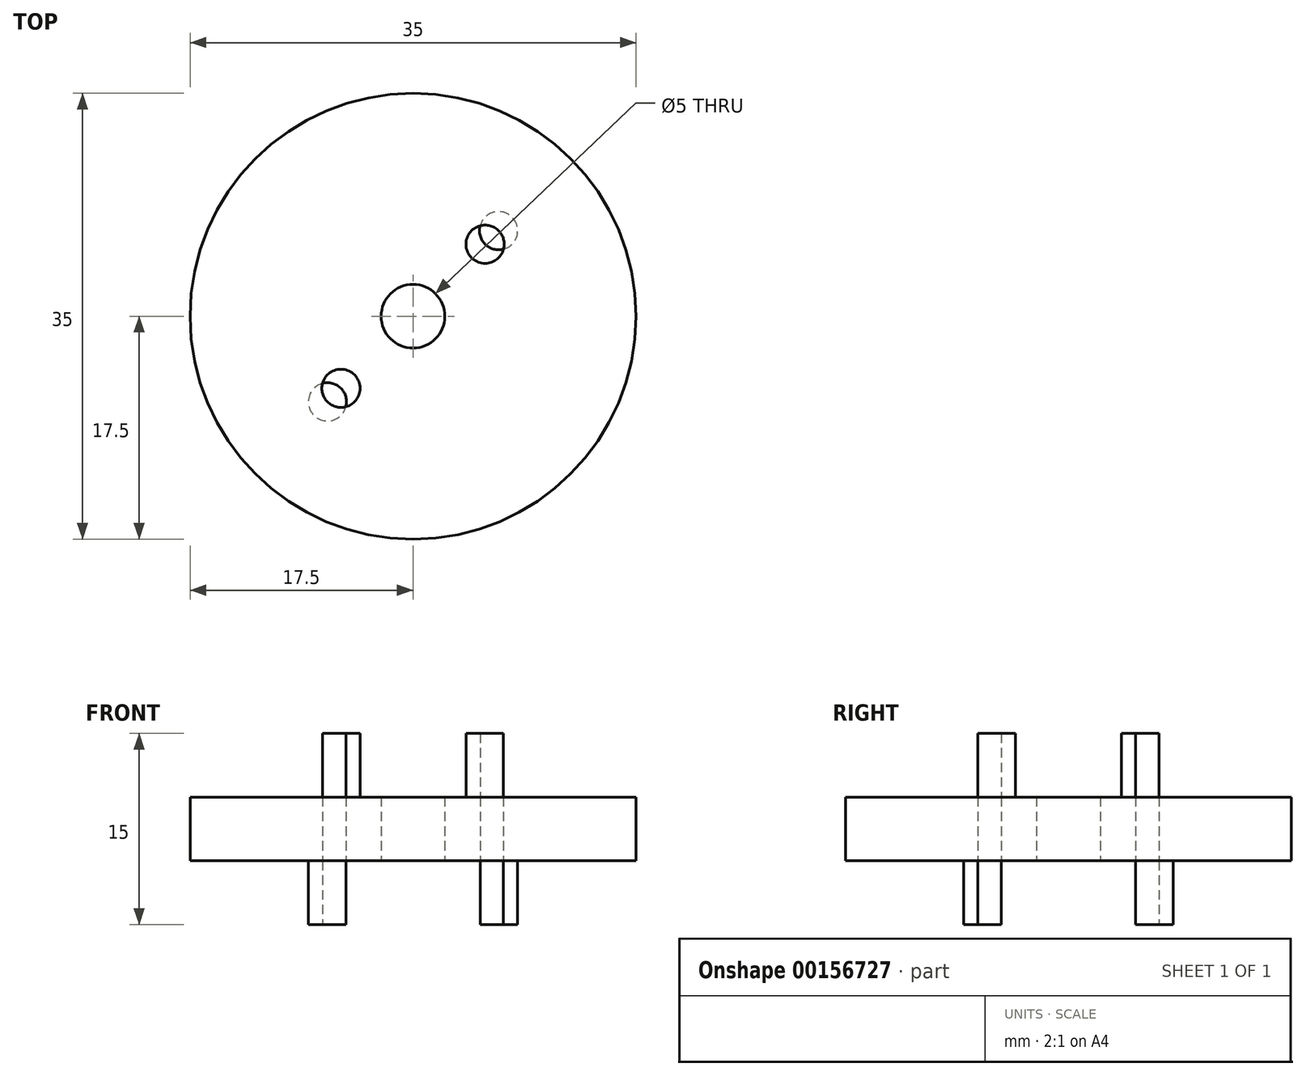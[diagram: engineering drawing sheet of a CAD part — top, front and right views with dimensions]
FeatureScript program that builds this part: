
annotation { "Feature Type Name" : "Feature", "Feature Type Description" : "" }
export const myFeature = defineFeature(function(context is Context, id is Id, definition is map)
    precondition{}
    {
        {
            var Q0;
            Q0=qCreatedBy(makeId("Top.planeOp"),FACE);
            var sketch = newSketch(context, id + "F0", { "sketchPlane" : qUnion([Q0])});
            skCircle(sketch, "E0", {"center": v(0, 0) * mm, "radius": 17.5 * mm});
            skCircle(sketch, "E1", {"center": v(0, 0) * mm, "radius": 2.5 * mm});
            skCircle(sketch, "E2", {"center": v(-5.66, 5.66) * mm, "radius": 1.5 * mm});
            skLineSegment(sketch, "E3", {"start": v(-5.66, 5.66) * mm, "end": v(0, 0) * mm, "construction": true});
            skCircle(sketch, "E4.MirrorC", {"center": v(5.66, 5.66) * mm, "radius": 1.5 * mm});
            skCircle(sketch, "E5.MirrorC", {"center": v(5.66, -5.66) * mm, "radius": 1.5 * mm});
            skCircle(sketch, "E6.MirrorC", {"center": v(-5.66, -5.66) * mm, "radius": 1.5 * mm});
            skCircle(sketch, "E7", {"center": v(0, 0) * mm, "radius": 9.5 * mm, "construction": true});
            skLineSegment(sketch, "E8", {"start": v(0, 0) * mm, "end": v(14.34, 14.34) * mm, "construction": true});
            skCircle(sketch, "E9", {"center": v(6.72, 6.72) * mm, "radius": 1.5 * mm});
            skCircle(sketch, "E10.MirrorC", {"center": v(-6.72, -6.72) * mm, "radius": 1.5 * mm});
            skSolve(sketch);
        }
        {
            var Q0;
            Q0=makeQuery(id+"F0.imprint","IMPRINT",FACE,{"disambiguationData":[TD([[makeQuery(id+"F0.imprint","IMPRINT",EDGE,{"derivedFrom":sQuery(id+"F0.wireOp",EDGE,"E0")}),1.0]])]});
            var Q1;
            Q1=makeQuery(id+"F0.imprint","IMPRINT",FACE,{"disambiguationData":[TD([[makeQuery(id+"F0.imprint","IMPRINT",EDGE,{"derivedFrom":sQuery(id+"F0.wireOp",EDGE,"E2")}),1.0]])]});
            var Q2;
            {var subQ0=sQuery(id+"F0.wireOp",EDGE,"E10.MirrorC");var subQ1=sQuery(id+"F0.wireOp",EDGE,"E6.MirrorC");var subQ2=makeQuery(id+"F0.imprint","INTERSECT",VERTEX,{"disambiguationData":[OD(0.0)],"derivedFrom":[subQ1,subQ0]});Q2=makeQuery(id+"F0.imprint","IMPRINT",FACE,{"disambiguationData":[TD([[makeQuery(id+"F0.imprint","IMPRINT",EDGE,{"disambiguationData":[TD([[subQ2,1.0]])],"derivedFrom":subQ1}),1.0]])]});}
            var Q3;
            {var subQ0=sQuery(id+"F0.wireOp",EDGE,"E10.MirrorC");var subQ1=sQuery(id+"F0.wireOp",EDGE,"E6.MirrorC");var subQ2=makeQuery(id+"F0.imprint","INTERSECT",VERTEX,{"disambiguationData":[OD(0.0)],"derivedFrom":[subQ1,subQ0]});Q3=makeQuery(id+"F0.imprint","IMPRINT",FACE,{"disambiguationData":[TD([[makeQuery(id+"F0.imprint","IMPRINT",EDGE,{"disambiguationData":[TD([[subQ2,1.0]])],"derivedFrom":subQ1}),-1.0]])]});}
            var Q4;
            {var subQ0=sQuery(id+"F0.wireOp",EDGE,"E10.MirrorC");var subQ1=sQuery(id+"F0.wireOp",EDGE,"E6.MirrorC");var subQ2=makeQuery(id+"F0.imprint","INTERSECT",VERTEX,{"disambiguationData":[OD(0.0)],"derivedFrom":[subQ1,subQ0]});Q4=makeQuery(id+"F0.imprint","IMPRINT",FACE,{"disambiguationData":[TD([[makeQuery(id+"F0.imprint","IMPRINT",EDGE,{"disambiguationData":[TD([[subQ2,-1.0]])],"derivedFrom":subQ1}),-1.0]])]});}
            var Q5;
            Q5=makeQuery(id+"F0.imprint","IMPRINT",FACE,{"disambiguationData":[TD([[makeQuery(id+"F0.imprint","IMPRINT",EDGE,{"derivedFrom":sQuery(id+"F0.wireOp",EDGE,"E5.MirrorC")}),1.0]])]});
            var Q6;
            {var subQ0=sQuery(id+"F0.wireOp",EDGE,"E9");var subQ1=sQuery(id+"F0.wireOp",EDGE,"E4.MirrorC");var subQ2=makeQuery(id+"F0.imprint","INTERSECT",VERTEX,{"disambiguationData":[OD(0.0)],"derivedFrom":[subQ1,subQ0]});Q6=makeQuery(id+"F0.imprint","IMPRINT",FACE,{"disambiguationData":[TD([[makeQuery(id+"F0.imprint","IMPRINT",EDGE,{"disambiguationData":[TD([[subQ2,1.0]])],"derivedFrom":subQ1}),-1.0]])]});}
            var Q7;
            {var subQ0=sQuery(id+"F0.wireOp",EDGE,"E9");var subQ1=sQuery(id+"F0.wireOp",EDGE,"E4.MirrorC");var subQ2=makeQuery(id+"F0.imprint","INTERSECT",VERTEX,{"disambiguationData":[OD(0.0)],"derivedFrom":[subQ1,subQ0]});Q7=makeQuery(id+"F0.imprint","IMPRINT",FACE,{"disambiguationData":[TD([[makeQuery(id+"F0.imprint","IMPRINT",EDGE,{"disambiguationData":[TD([[subQ2,-1.0]])],"derivedFrom":subQ1}),-1.0]])]});}
            var Q8;
            {var subQ0=sQuery(id+"F0.wireOp",EDGE,"E9");var subQ1=sQuery(id+"F0.wireOp",EDGE,"E4.MirrorC");var subQ2=makeQuery(id+"F0.imprint","INTERSECT",VERTEX,{"disambiguationData":[OD(0.0)],"derivedFrom":[subQ1,subQ0]});Q8=makeQuery(id+"F0.imprint","IMPRINT",FACE,{"disambiguationData":[TD([[makeQuery(id+"F0.imprint","IMPRINT",EDGE,{"disambiguationData":[TD([[subQ2,-1.0]])],"derivedFrom":subQ1}),1.0]])]});}
            extrude(context, id + "F1", {"entities" : qUnion([Q0, Q1, Q2, Q3, Q4, Q5, Q6, Q7, Q8]), "depth" : 15 * mm});
        }
        {
            var Q0;
            Q0=makeQuery(id+"F0.imprint","IMPRINT",FACE,{"disambiguationData":[TD([[makeQuery(id+"F0.imprint","IMPRINT",EDGE,{"derivedFrom":sQuery(id+"F0.wireOp",EDGE,"E2")}),1.0]])]});
            var Q1;
            {var subQ0=sQuery(id+"F0.wireOp",EDGE,"E9");var subQ1=sQuery(id+"F0.wireOp",EDGE,"E4.MirrorC");var subQ2=makeQuery(id+"F0.imprint","INTERSECT",VERTEX,{"disambiguationData":[OD(0.0)],"derivedFrom":[subQ1,subQ0]});Q1=makeQuery(id+"F0.imprint","IMPRINT",FACE,{"disambiguationData":[TD([[makeQuery(id+"F0.imprint","IMPRINT",EDGE,{"disambiguationData":[TD([[subQ2,1.0]])],"derivedFrom":subQ1}),-1.0]])]});}
            var Q2;
            {var subQ0=sQuery(id+"F0.wireOp",EDGE,"E9");var subQ1=sQuery(id+"F0.wireOp",EDGE,"E4.MirrorC");var subQ2=makeQuery(id+"F0.imprint","INTERSECT",VERTEX,{"disambiguationData":[OD(0.0)],"derivedFrom":[subQ1,subQ0]});Q2=makeQuery(id+"F0.imprint","IMPRINT",FACE,{"disambiguationData":[TD([[makeQuery(id+"F0.imprint","IMPRINT",EDGE,{"disambiguationData":[TD([[subQ2,-1.0]])],"derivedFrom":subQ1}),-1.0]])]});}
            var Q3;
            Q3=makeQuery(id+"F0.imprint","IMPRINT",FACE,{"disambiguationData":[TD([[makeQuery(id+"F0.imprint","IMPRINT",EDGE,{"derivedFrom":sQuery(id+"F0.wireOp",EDGE,"E5.MirrorC")}),1.0]])]});
            var Q4;
            {var subQ0=sQuery(id+"F0.wireOp",EDGE,"E10.MirrorC");var subQ1=sQuery(id+"F0.wireOp",EDGE,"E6.MirrorC");var subQ2=makeQuery(id+"F0.imprint","INTERSECT",VERTEX,{"disambiguationData":[OD(0.0)],"derivedFrom":[subQ1,subQ0]});Q4=makeQuery(id+"F0.imprint","IMPRINT",FACE,{"disambiguationData":[TD([[makeQuery(id+"F0.imprint","IMPRINT",EDGE,{"disambiguationData":[TD([[subQ2,-1.0]])],"derivedFrom":subQ1}),-1.0]])]});}
            var Q5;
            {var subQ0=sQuery(id+"F0.wireOp",EDGE,"E10.MirrorC");var subQ1=sQuery(id+"F0.wireOp",EDGE,"E6.MirrorC");var subQ2=makeQuery(id+"F0.imprint","INTERSECT",VERTEX,{"disambiguationData":[OD(0.0)],"derivedFrom":[subQ1,subQ0]});Q5=makeQuery(id+"F0.imprint","IMPRINT",FACE,{"disambiguationData":[TD([[makeQuery(id+"F0.imprint","IMPRINT",EDGE,{"disambiguationData":[TD([[subQ2,1.0]])],"derivedFrom":subQ1}),-1.0]])]});}
            extrude(context, id + "F2", {"entities" : qUnion([Q0, Q1, Q2, Q3, Q4, Q5]), "operationType" : NewBodyOperationType.REMOVE, "depth" : 25 * mm, "hasSecondDirection" : true, "secondDirectionOppositeDirection" : false, "secondDirectionDepth" : 10 * mm});
        }
        {
            var Q0;
            Q0=makeQuery(id+"F0.imprint","IMPRINT",FACE,{"disambiguationData":[TD([[makeQuery(id+"F0.imprint","IMPRINT",EDGE,{"derivedFrom":sQuery(id+"F0.wireOp",EDGE,"E2")}),1.0]])]});
            var Q1;
            Q1=makeQuery(id+"F0.imprint","IMPRINT",FACE,{"disambiguationData":[TD([[makeQuery(id+"F0.imprint","IMPRINT",EDGE,{"derivedFrom":sQuery(id+"F0.wireOp",EDGE,"E5.MirrorC")}),1.0]])]});
            var Q2;
            {var subQ0=sQuery(id+"F0.wireOp",EDGE,"E10.MirrorC");var subQ1=sQuery(id+"F0.wireOp",EDGE,"E6.MirrorC");var subQ2=makeQuery(id+"F0.imprint","INTERSECT",VERTEX,{"disambiguationData":[OD(0.0)],"derivedFrom":[subQ1,subQ0]});Q2=makeQuery(id+"F0.imprint","IMPRINT",FACE,{"disambiguationData":[TD([[makeQuery(id+"F0.imprint","IMPRINT",EDGE,{"disambiguationData":[TD([[subQ2,1.0]])],"derivedFrom":subQ1}),1.0]])]});}
            var Q3;
            {var subQ0=sQuery(id+"F0.wireOp",EDGE,"E10.MirrorC");var subQ1=sQuery(id+"F0.wireOp",EDGE,"E6.MirrorC");var subQ2=makeQuery(id+"F0.imprint","INTERSECT",VERTEX,{"disambiguationData":[OD(0.0)],"derivedFrom":[subQ1,subQ0]});Q3=makeQuery(id+"F0.imprint","IMPRINT",FACE,{"disambiguationData":[TD([[makeQuery(id+"F0.imprint","IMPRINT",EDGE,{"disambiguationData":[TD([[subQ2,1.0]])],"derivedFrom":subQ1}),-1.0]])]});}
            var Q4;
            {var subQ0=sQuery(id+"F0.wireOp",EDGE,"E9");var subQ1=sQuery(id+"F0.wireOp",EDGE,"E4.MirrorC");var subQ2=makeQuery(id+"F0.imprint","INTERSECT",VERTEX,{"disambiguationData":[OD(0.0)],"derivedFrom":[subQ1,subQ0]});Q4=makeQuery(id+"F0.imprint","IMPRINT",FACE,{"disambiguationData":[TD([[makeQuery(id+"F0.imprint","IMPRINT",EDGE,{"disambiguationData":[TD([[subQ2,-1.0]])],"derivedFrom":subQ1}),1.0]])]});}
            var Q5;
            {var subQ0=sQuery(id+"F0.wireOp",EDGE,"E9");var subQ1=sQuery(id+"F0.wireOp",EDGE,"E4.MirrorC");var subQ2=makeQuery(id+"F0.imprint","INTERSECT",VERTEX,{"disambiguationData":[OD(0.0)],"derivedFrom":[subQ1,subQ0]});Q5=makeQuery(id+"F0.imprint","IMPRINT",FACE,{"disambiguationData":[TD([[makeQuery(id+"F0.imprint","IMPRINT",EDGE,{"disambiguationData":[TD([[subQ2,-1.0]])],"derivedFrom":subQ1}),-1.0]])]});}
            extrude(context, id + "F3", {"entities" : qUnion([Q0, Q1, Q2, Q3, Q4, Q5]), "operationType" : NewBodyOperationType.REMOVE, "depth" : 5 * mm, "hasSecondDirection" : true, "secondDirectionOppositeDirection" : true, "secondDirectionDepth" : 2 * mm});
        }
    });
